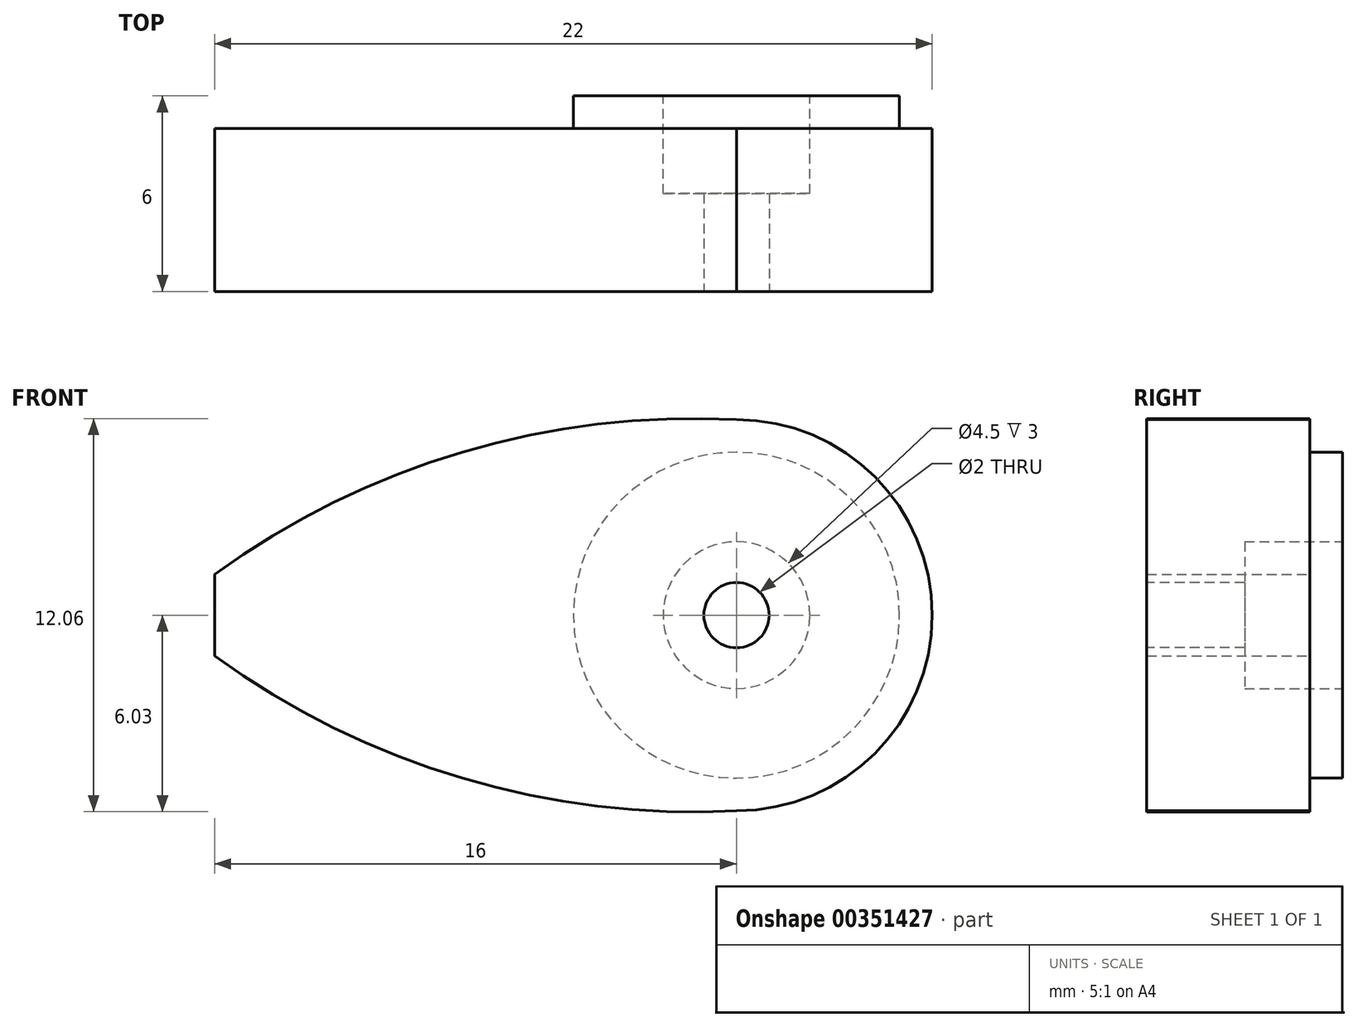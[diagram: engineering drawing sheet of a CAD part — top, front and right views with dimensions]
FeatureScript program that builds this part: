
annotation { "Feature Type Name" : "Feature", "Feature Type Description" : "" }
export const myFeature = defineFeature(function(context is Context, id is Id, definition is map)
    precondition{}
    {
        {
            var Q0;
            Q0=qCreatedBy(makeId("Front.planeOp"),FACE);
            var sketch = newSketch(context, id + "F0", { "sketchPlane" : qUnion([Q0])});
            skCircle(sketch, "E0", {"center": v(0, 0) * mm, "radius": 5 * mm});
            skSolve(sketch);
        }
        {
            var Q0;
            Q0=qSketchRegion(id+"F0",true);
            extrude(context, id + "F1", {"entities" : qUnion([Q0]), "depth" : 1 * mm});
        }
        {
            var Q0;
            Q0=makeQuery(id+"F1.opExtrude","CAP_FACE",FACE,{"disambiguationData":[OSD([sQuery(id+"F0.wireOp",EDGE,"eqiGtoLe-QH7P-NGeF-8R8m-luKEqvCLz7Ql"),sQuery(id+"F0.wireOp",EDGE,"E0")])],"isStart":false});
            var sketch = newSketch(context, id + "F2", { "sketchPlane" : qUnion([Q0])});
            skCircle(sketch, "E1", {"center": v(0, 0) * mm, "radius": 6 * mm});
            skLineSegment(sketch, "E2", {"start": v(-6, 0) * mm, "end": v(-16, 0) * mm});
            skLineSegment(sketch, "E3.bottom", {"start": v(-16, 1.25) * mm, "end": v(4, 1.25) * mm});
            skLineSegment(sketch, "E3.top", {"start": v(-16, -1.25) * mm, "end": v(4, -1.25) * mm});
            skLineSegment(sketch, "E3.left", {"start": v(-16, 1.25) * mm, "end": v(-16, -1.25) * mm});
            skLineSegment(sketch, "E3.right", {"start": v(4, 1.25) * mm, "end": v(4, -1.25) * mm});
            skPoint(sketch, "E3.middle", {"position": v(-6, 0) * mm});
            skArc(sketch, "E4", {"start": v(0, 6) * mm, "mid": v(-8.4, 5) * mm, "end": v(-16, 1.25) * mm});
            skArc(sketch, "E5", {"start": v(-16, -1.25) * mm, "mid": v(-8.4, -5) * mm, "end": v(0, -6) * mm});
            skSolve(sketch);
        }
        {
            var Q0;
            Q0=qSketchRegion(id+"F2",true);
            extrude(context, id + "F3", {"entities" : qUnion([Q0]), "operationType" : NewBodyOperationType.ADD, "depth" : 5 * mm});
        }
        {
            var Q0;
            Q0=makeQuery(id+"F3.opExtrude","CAP_FACE",FACE,{"disambiguationData":[OSD([sQuery(id+"F2.wireOp",EDGE,"E1"),sQuery(id+"F2.wireOp",EDGE,"E3.bottom"),sQuery(id+"F2.wireOp",EDGE,"E3.top"),sQuery(id+"F2.wireOp",EDGE,"E3.left"),sQuery(id+"F2.wireOp",EDGE,"E3.right"),sQuery(id+"F2.wireOp",EDGE,"E4"),sQuery(id+"F2.wireOp",EDGE,"E5")])],"isStart":false});
            var sketch = newSketch(context, id + "F4", { "sketchPlane" : qUnion([Q0])});
            skLineSegment(sketch, "E6.bottom", {"start": v(-6.69, 1.86) * mm, "end": v(4.64, 1.86) * mm});
            skLineSegment(sketch, "E6.top", {"start": v(-6.69, -1.88) * mm, "end": v(4.64, -1.88) * mm});
            skLineSegment(sketch, "E6.left", {"start": v(-6.69, 1.86) * mm, "end": v(-6.69, -1.88) * mm});
            skLineSegment(sketch, "E6.right", {"start": v(4.64, 1.86) * mm, "end": v(4.64, -1.88) * mm});
            skSolve(sketch);
        }
        {
            var Q0;
            Q0=qSketchRegion(id+"F4",true);
            extrude(context, id + "F5", {"entities" : qUnion([Q0]), "operationType" : NewBodyOperationType.ADD, "oppositeDirection" : true, "depth" : 5 * mm});
        }
        {
            var Q0;
            Q0=makeQuery(id+"F1.opExtrude","CAP_FACE",FACE,{"disambiguationData":[OSD([sQuery(id+"F0.wireOp",EDGE,"E0")])],"isStart":true});
            var sketch = newSketch(context, id + "F6", { "sketchPlane" : qUnion([Q0])});
            skCircle(sketch, "E7", {"center": v(0, 0) * mm, "radius": 2.25 * mm});
            skSolve(sketch);
        }
        {
            var Q0;
            Q0=qSketchRegion(id+"F6",true);
            extrude(context, id + "F7", {"entities" : qUnion([Q0]), "operationType" : NewBodyOperationType.REMOVE, "oppositeDirection" : true, "depth" : 3 * mm});
        }
        {
            var Q0;
            Q0=makeQuery(id+"F5.boolean.opBoolean","MERGE",FACE,{"derivedFrom":[makeQuery(id+"F3.opExtrude","CAP_FACE",FACE,{"disambiguationData":[OSD([sQuery(id+"F2.wireOp",EDGE,"E1"),sQuery(id+"F2.wireOp",EDGE,"E3.bottom"),sQuery(id+"F2.wireOp",EDGE,"E3.top"),sQuery(id+"F2.wireOp",EDGE,"E3.left"),sQuery(id+"F2.wireOp",EDGE,"E3.right"),sQuery(id+"F2.wireOp",EDGE,"E4"),sQuery(id+"F2.wireOp",EDGE,"E5")])],"isStart":false}),makeQuery(id+"F5.opExtrude","CAP_FACE",FACE,{"disambiguationData":[OSD([sQuery(id+"F4.wireOp",EDGE,"E6.bottom"),sQuery(id+"F4.wireOp",EDGE,"E6.top"),sQuery(id+"F4.wireOp",EDGE,"E6.left"),sQuery(id+"F4.wireOp",EDGE,"E6.right")])],"isStart":true})]});
            var sketch = newSketch(context, id + "F8", { "sketchPlane" : qUnion([Q0])});
            skCircle(sketch, "E8", {"center": v(0, 0) * mm, "radius": 1 * mm});
            skSolve(sketch);
        }
        {
            var Q0;
            Q0=qSketchRegion(id+"F8",true);
            extrude(context, id + "F9", {"entities" : qUnion([Q0]), "operationType" : NewBodyOperationType.REMOVE, "oppositeDirection" : true, "depth" : 25 * mm});
        }
    });
